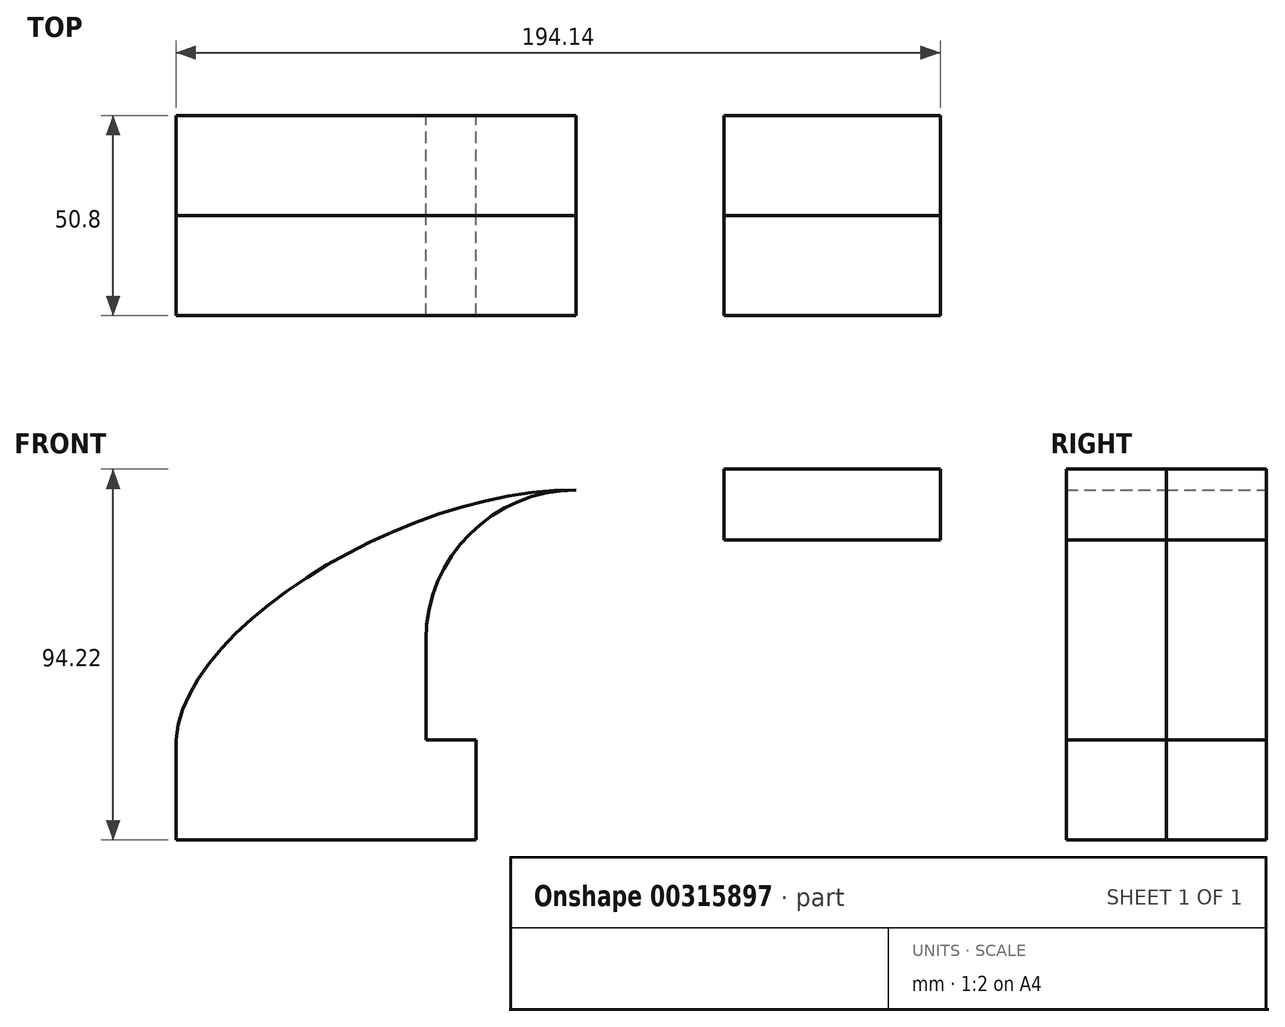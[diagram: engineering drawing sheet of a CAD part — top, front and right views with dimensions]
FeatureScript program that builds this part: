
annotation { "Feature Type Name" : "Feature", "Feature Type Description" : "" }
export const myFeature = defineFeature(function(context is Context, id is Id, definition is map)
    precondition{}
    {
        {
            var Q0;
            Q0=qCreatedBy(makeId("Front.planeOp"),FACE);
            var sketch = newSketch(context, id + "F0", { "sketchPlane" : qUnion([Q0])});
            skLineSegment(sketch, "E0.bottom", {"start": v(-38.1, -12.7) * mm, "end": v(38.1, -12.7) * mm});
            skLineSegment(sketch, "E0.top", {"start": v(-38.1, 12.7) * mm, "end": v(38.1, 12.7) * mm});
            skLineSegment(sketch, "E0.left", {"start": v(-38.1, -12.7) * mm, "end": v(-38.1, 12.7) * mm});
            skLineSegment(sketch, "E0.right", {"start": v(38.1, -12.7) * mm, "end": v(38.1, 12.7) * mm});
            skPoint(sketch, "E0.middle", {"position": v(0, 0) * mm});
            skLineSegment(sketch, "E1.bottom", {"start": v(101.14, 81.52) * mm, "end": v(156.04, 81.52) * mm});
            skLineSegment(sketch, "E1.top", {"start": v(101.14, 63.5) * mm, "end": v(156.04, 63.5) * mm});
            skLineSegment(sketch, "E1.left", {"start": v(101.14, 81.52) * mm, "end": v(101.14, 63.5) * mm});
            skLineSegment(sketch, "E1.right", {"start": v(156.04, 81.52) * mm, "end": v(156.04, 63.5) * mm});
            skPoint(sketch, "E1.middle", {"position": v(128.6, 72.51) * mm});
            skLineSegment(sketch, "E2", {"start": v(38.1, 12.7) * mm, "end": v(38.1, 38.1) * mm});
            skLineSegment(sketch, "E3", {"start": v(63.5, 63.5) * mm, "end": v(101.14, 63.5) * mm});
            skArc(sketch, "E4", {"start": v(63.5, 63.5) * mm, "mid": v(45.54, 56.06) * mm, "end": v(38.1, 38.1) * mm});
            skLineSegment(sketch, "E5.0", {"start": v(44.45, 12.7) * mm, "end": v(44.45, 38.1) * mm});
            skLineSegment(sketch, "E6.0", {"start": v(63.5, 76.2) * mm, "end": v(100.85, 76.2) * mm});
            skArc(sketch, "E6.1", {"start": v(63.5, 76.2) * mm, "mid": v(36.56, 65.04) * mm, "end": v(25.4, 38.1) * mm});
            skLineSegment(sketch, "E6.2", {"start": v(25.4, 12.7) * mm, "end": v(25.4, 38.1) * mm});
            skFitSpline(sketch, "E7", {"points": [v(63.5, 76.2) * mm, v(-38.1, 12.7) * mm], "startDerivative": vector(-126.55, 1.21) * mm, "endDerivative": vector(-5.5, -87.36) * mm});
            skSolve(sketch);
        }
        {
            var Q0;
            Q0=makeQuery(id+"F0.imprint","IMPRINT",FACE,{"disambiguationData":[TD([[makeQuery(id+"F0.imprint","IMPRINT",EDGE,{"derivedFrom":sQuery(id+"F0.wireOp",EDGE,"E6.1")}),-1.0]])]});
            var Q1;
            Q1=makeQuery(id+"F0.imprint","IMPRINT",FACE,{"disambiguationData":[TD([[makeQuery(id+"F0.imprint","IMPRINT",EDGE,{"derivedFrom":sQuery(id+"F0.wireOp",EDGE,"E0.bottom")}),1.0]])]});
            var Q2;
            Q2=makeQuery(id+"F0.imprint","IMPRINT",FACE,{"disambiguationData":[TD([[makeQuery(id+"F0.imprint","IMPRINT",EDGE,{"derivedFrom":sQuery(id+"F0.wireOp",EDGE,"E1.bottom")}),-1.0]])]});
            extrude(context, id + "F1", {"entities" : qUnion([Q0, Q1, Q2]), "depth" : 25.4 * mm});
        }
        {
            var Q0;
            Q0=makeQuery(id+"F1.opExtrude","CAP_FACE",FACE,{"disambiguationData":[OSD([sQuery(id+"F0.wireOp",EDGE,"E1.bottom"),sQuery(id+"F0.wireOp",EDGE,"E1.top"),sQuery(id+"F0.wireOp",EDGE,"E1.left"),sQuery(id+"F0.wireOp",EDGE,"E1.right")])],"isStart":false});
            var Q1;
            Q1=makeQuery(id+"F1.opExtrude","CAP_FACE",FACE,{"disambiguationData":[OSD([sQuery(id+"F0.wireOp",EDGE,"E0.bottom"),sQuery(id+"F0.wireOp",EDGE,"E0.top"),sQuery(id+"F0.wireOp",EDGE,"E0.left"),sQuery(id+"F0.wireOp",EDGE,"E0.right"),sQuery(id+"F0.wireOp",EDGE,"E6.1"),sQuery(id+"F0.wireOp",EDGE,"E6.2"),sQuery(id+"F0.wireOp",EDGE,"E7")])],"isStart":false});
            extrude(context, id + "F2", {"entities" : qUnion([Q0, Q1]), "depth" : 25.4 * mm});
        }
    });
